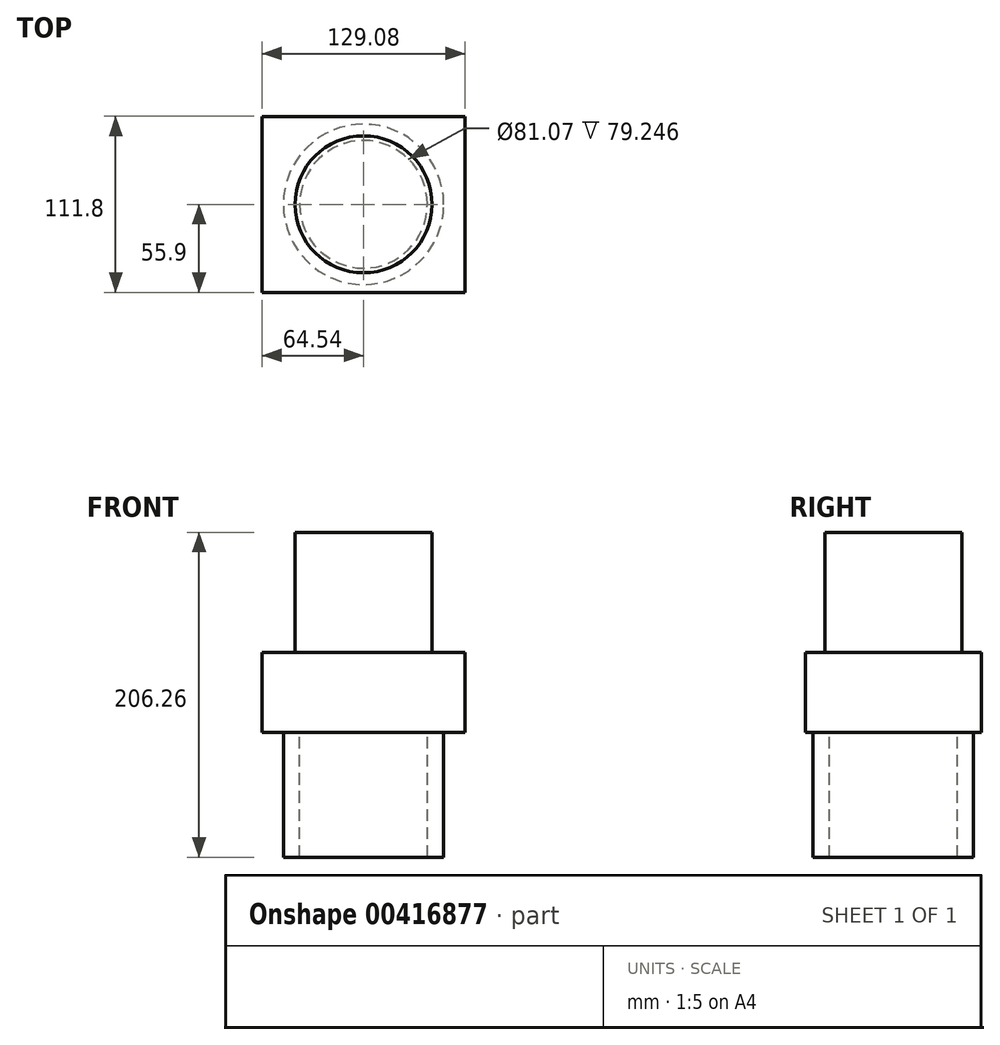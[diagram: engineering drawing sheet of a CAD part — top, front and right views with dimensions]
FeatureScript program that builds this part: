
annotation { "Feature Type Name" : "Feature", "Feature Type Description" : "" }
export const myFeature = defineFeature(function(context is Context, id is Id, definition is map)
    precondition{}
    {
        {
            var Q0;
            Q0=qCreatedBy(makeId("Top.planeOp"),FACE);
            var sketch = newSketch(context, id + "F0", { "sketchPlane" : qUnion([Q0])});
            skLineSegment(sketch, "E0.bottom", {"start": v(-64.54, 55.9) * mm, "end": v(64.54, 55.9) * mm});
            skLineSegment(sketch, "E0.top", {"start": v(-64.54, -55.9) * mm, "end": v(64.54, -55.9) * mm});
            skLineSegment(sketch, "E0.left", {"start": v(-64.54, 55.9) * mm, "end": v(-64.54, -55.9) * mm});
            skLineSegment(sketch, "E0.right", {"start": v(64.54, 55.9) * mm, "end": v(64.54, -55.9) * mm});
            skPoint(sketch, "E0.middle", {"position": v(0, 0) * mm});
            skSolve(sketch);
        }
        {
            var Q0;
            Q0 = qSketchRegion(id + "F0", true);
            extrude(context, id + "F1", {"entities" : qUnion([Q0]), "oppositeDirection" : true, "depth" : 50.81 * mm});
        }
        {
            var Q0;
            Q0=makeQuery(id+"F1.opExtrude","CAP_FACE",FACE,{"disambiguationData":[OSD([sQuery(id+"F0.wireOp",EDGE,"E0.bottom"),sQuery(id+"F0.wireOp",EDGE,"E0.top"),sQuery(id+"F0.wireOp",EDGE,"E0.left"),sQuery(id+"F0.wireOp",EDGE,"E0.right")])],"isStart":true});
            var sketch = newSketch(context, id + "F2", { "sketchPlane" : qUnion([Q0])});
            skCircle(sketch, "E1", {"center": v(0, 0) * mm, "radius": 43.46 * mm});
            skSolve(sketch);
        }
        {
            var Q0;
            Q0 = qSketchRegion(id + "F2", true);
            extrude(context, id + "F3", {"entities" : qUnion([Q0]), "operationType" : NewBodyOperationType.ADD, "depth" : 76.2 * mm});
        }
        {
            var Q0;
            Q0=makeQuery(id+"F1.opExtrude","CAP_FACE",FACE,{"disambiguationData":[OSD([sQuery(id+"F0.wireOp",EDGE,"E0.bottom"),sQuery(id+"F0.wireOp",EDGE,"E0.top"),sQuery(id+"F0.wireOp",EDGE,"E0.left"),sQuery(id+"F0.wireOp",EDGE,"E0.right")])],"isStart":false});
            var sketch = newSketch(context, id + "F4", { "sketchPlane" : qUnion([Q0])});
            skCircle(sketch, "E2", {"center": v(0, 0) * mm, "radius": 50.95 * mm});
            skCircle(sketch, "E3", {"center": v(0, 0) * mm, "radius": 40.54 * mm});
            skSolve(sketch);
        }
        {
            var Q0;
            Q0 = qSketchRegion(id + "F4", true);
            extrude(context, id + "F5", {"entities" : qUnion([Q0]), "operationType" : NewBodyOperationType.ADD, "depth" : 79.25 * mm});
        }
    });
